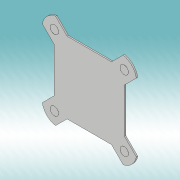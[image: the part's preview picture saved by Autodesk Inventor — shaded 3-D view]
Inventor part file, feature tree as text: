
AUTODESK INVENTOR PART (.ipt)
format: ipt  version: 2019 (Build 230136000, 136)  size: 131,584 bytes
history: native  units: mm
features: extrude x2, sketch x1
ambient origin geometry x8: Origin, YZ Plane, XZ Plane, XY Plane, X Axis, Y Axis, Z Axis, Center Point
bodies: Solid1 (feature_tree)
feature tree (3):
  sketch  "Sketch1"  dims[d0=135.0deg d1=47.5mm d2=35.0mm d3=40.0mm d4=75.0mm d5=35.0mm d6=66.0mm d7=1.5mm d8=1.5mm d9=0.0mm d10=0.0mm d11=20.0mm d12=38.0mm d13=18.0mm d14=1.6mm d15=0.0mm]
  extrude  "Extrusion1"  Depth=47.5mm
  extrude  "Extrusion2"  Depth=35.0mm
